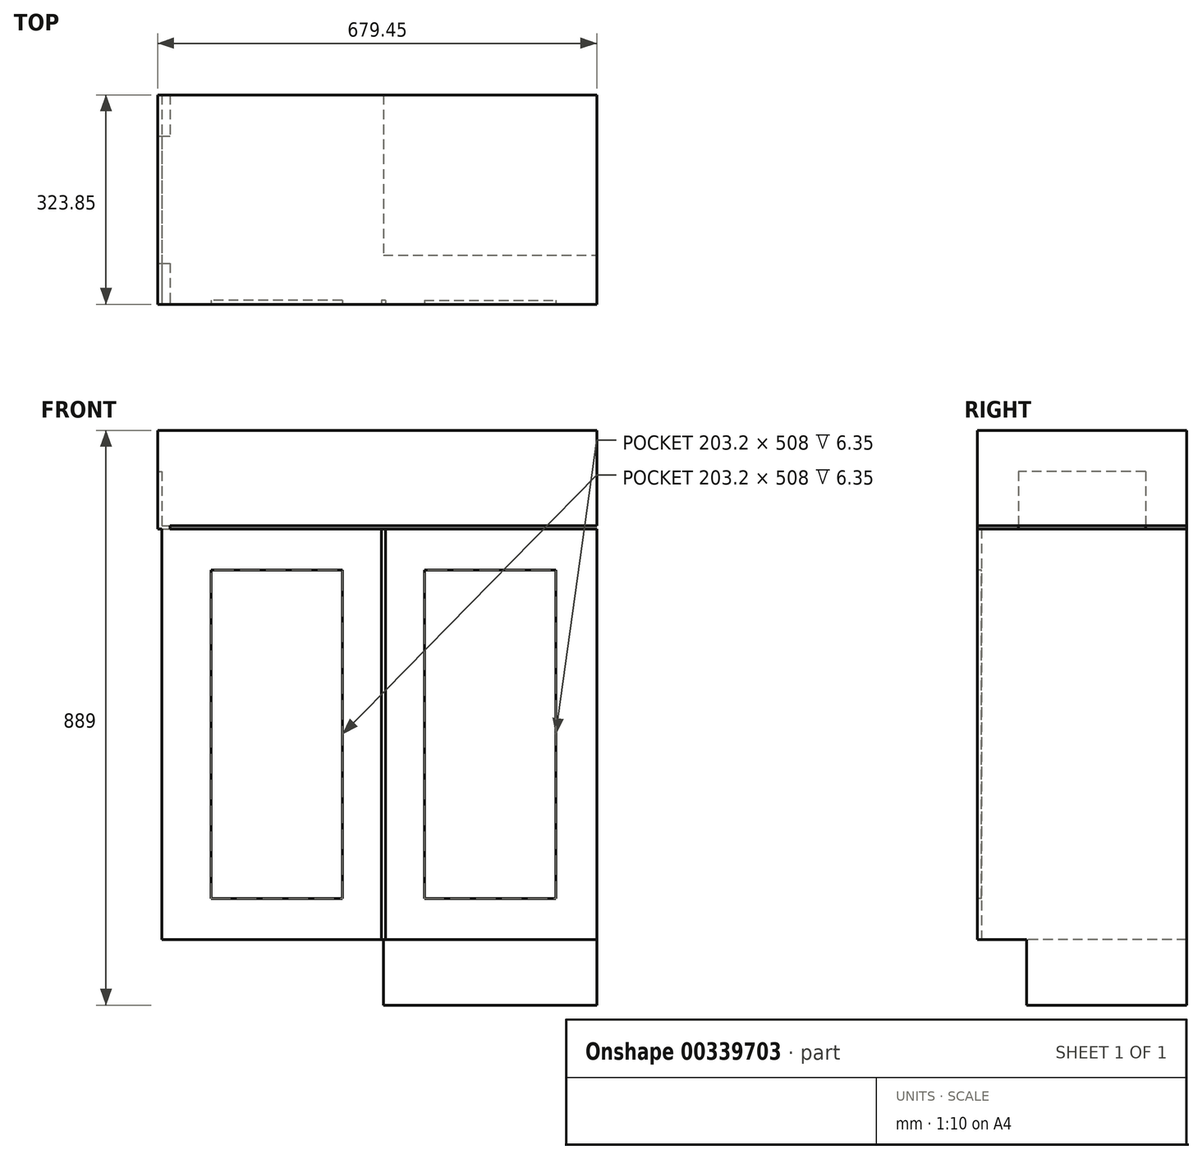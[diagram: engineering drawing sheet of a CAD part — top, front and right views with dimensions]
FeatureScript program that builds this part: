
annotation { "Feature Type Name" : "Feature", "Feature Type Description" : "" }
export const myFeature = defineFeature(function(context is Context, id is Id, definition is map)
    precondition{}
    {
        {
            var Q0;
            Q0=qCreatedBy(makeId("Front.planeOp"),FACE);
            var sketch = newSketch(context, id + "F0", { "sketchPlane" : qUnion([Q0])});
            skLineSegment(sketch, "E0.bottom", {"start": v(0, 0) * mm, "end": v(-330.2, 0) * mm});
            skLineSegment(sketch, "E0.top", {"start": v(0, 635) * mm, "end": v(-330.2, 635) * mm});
            skLineSegment(sketch, "E0.left", {"start": v(0, 0) * mm, "end": v(0, 635) * mm});
            skLineSegment(sketch, "E0.right", {"start": v(-330.2, 0) * mm, "end": v(-330.2, 635) * mm});
            skLineSegment(sketch, "E1.0", {"start": v(-63.5, 571.5) * mm, "end": v(-266.7, 571.5) * mm});
            skLineSegment(sketch, "E1.1", {"start": v(-63.5, 63.5) * mm, "end": v(-63.5, 571.5) * mm});
            skLineSegment(sketch, "E1.2", {"start": v(-63.5, 63.5) * mm, "end": v(-266.7, 63.5) * mm});
            skLineSegment(sketch, "E1.3", {"start": v(-266.7, 63.5) * mm, "end": v(-266.7, 571.5) * mm});
            skLineSegment(sketch, "E2.bottom", {"start": v(-330.2, 0) * mm, "end": v(0, 0) * mm});
            skLineSegment(sketch, "E2.top", {"start": v(-330.2, -101.6) * mm, "end": v(0, -101.6) * mm});
            skLineSegment(sketch, "E2.left", {"start": v(-330.2, 0) * mm, "end": v(-330.2, -101.6) * mm});
            skLineSegment(sketch, "E2.right", {"start": v(0, 0) * mm, "end": v(0, -101.6) * mm});
            skLineSegment(sketch, "E3.bottom", {"start": v(-330.2, 635) * mm, "end": v(0, 635) * mm});
            skLineSegment(sketch, "E3.top", {"start": v(-330.2, 787.4) * mm, "end": v(0, 787.4) * mm});
            skLineSegment(sketch, "E3.left", {"start": v(-330.2, 635) * mm, "end": v(-330.2, 787.4) * mm});
            skLineSegment(sketch, "E3.right", {"start": v(0, 635) * mm, "end": v(0, 787.4) * mm});
            skLineSegment(sketch, "E4.top", {"start": v(-330.2, 640.08) * mm, "end": v(0, 640.08) * mm});
            skLineSegment(sketch, "E4.left", {"start": v(-330.2, 635) * mm, "end": v(-330.2, 640.08) * mm});
            skLineSegment(sketch, "E4.right", {"start": v(0, 635) * mm, "end": v(0, 640.08) * mm});
            skLineSegment(sketch, "E5.MirrorCS", {"start": v(330.2, 635) * mm, "end": v(330.2, 640.08) * mm});
            skLineSegment(sketch, "E6.MirrorCS", {"start": v(0, 635) * mm, "end": v(330.2, 635) * mm});
            skLineSegment(sketch, "E7.MirrorCS", {"start": v(330.2, 635) * mm, "end": v(0, 635) * mm});
            skLineSegment(sketch, "E8.MirrorCS", {"start": v(0, 0) * mm, "end": v(330.2, 0) * mm});
            skLineSegment(sketch, "E9.MirrorCS", {"start": v(330.2, 0) * mm, "end": v(330.2, -101.6) * mm});
            skLineSegment(sketch, "E10.MirrorCS", {"start": v(330.2, -101.6) * mm, "end": v(0, -101.6) * mm});
            skLineSegment(sketch, "E11.MirrorCS", {"start": v(330.2, 0) * mm, "end": v(0, 0) * mm});
            skLineSegment(sketch, "E12.MirrorCS", {"start": v(266.7, 63.5) * mm, "end": v(266.7, 571.5) * mm});
            skLineSegment(sketch, "E13.MirrorCS", {"start": v(63.5, 63.5) * mm, "end": v(266.7, 63.5) * mm});
            skLineSegment(sketch, "E14.MirrorCS", {"start": v(63.5, 63.5) * mm, "end": v(63.5, 571.5) * mm});
            skLineSegment(sketch, "E15.MirrorCS", {"start": v(63.5, 571.5) * mm, "end": v(266.7, 571.5) * mm});
            skLineSegment(sketch, "E16.MirrorCS", {"start": v(330.2, 0) * mm, "end": v(330.2, 635) * mm});
            skLineSegment(sketch, "E17.MirrorCS", {"start": v(330.2, 635) * mm, "end": v(330.2, 787.4) * mm});
            skLineSegment(sketch, "E18.MirrorCS", {"start": v(330.2, 640.08) * mm, "end": v(0, 640.08) * mm});
            skLineSegment(sketch, "E19.MirrorCS", {"start": v(330.2, 787.4) * mm, "end": v(0, 787.4) * mm});
            skLineSegment(sketch, "E20", {"start": v(-3.18, 635) * mm, "end": v(-3.17, 0) * mm});
            skLineSegment(sketch, "E21", {"start": v(3.17, 635) * mm, "end": v(3.18, 0) * mm});
            skSolve(sketch);
        }
        {
            var Q0;
            Q0=makeQuery(id+"F0.imprint","IMPRINT",FACE,{"disambiguationData":[TD([[makeQuery(id+"F0.imprint","IMPRINT",EDGE,{"derivedFrom":sQuery(id+"F0.wireOp",EDGE,"E1.0")}),1.0]])]});
            var Q1;
            Q1=makeQuery(id+"F0.imprint","IMPRINT",FACE,{"disambiguationData":[TD([[makeQuery(id+"F0.imprint","IMPRINT",EDGE,{"derivedFrom":sQuery(id+"F0.wireOp",EDGE,"E2.bottom")}),-1.0]])]});
            var Q2;
            Q2=makeQuery(id+"F0.imprint","IMPRINT",FACE,{"disambiguationData":[TD([[makeQuery(id+"F0.imprint","IMPRINT",EDGE,{"derivedFrom":sQuery(id+"F0.wireOp",EDGE,"E0.left")}),1.0]])]});
            var Q3;
            {var subQ0=sQuery(id+"F0.wireOp",EDGE,"E3.top");Q3=makeQuery(id+"F0.imprint","IMPRINT",FACE,{"disambiguationData":[TD([[makeQuery(id+"F0.imprint","IMPRINT",EDGE,{"derivedFrom":subQ0}),-1.0]])]});}
            var Q4;
            {var subQ0=sQuery(id+"F0.wireOp",EDGE,"E3.bottom");Q4=makeQuery(id+"F0.imprint","IMPRINT",FACE,{"disambiguationData":[TD([[makeQuery(id+"F0.imprint","IMPRINT",EDGE,{"derivedFrom":subQ0}),1.0]])]});}
            var Q5;
            Q5=makeQuery(id+"F0.imprint","IMPRINT",FACE,{"disambiguationData":[TD([[makeQuery(id+"F0.imprint","IMPRINT",EDGE,{"derivedFrom":sQuery(id+"F0.wireOp",EDGE,"E12.MirrorCS")}),1.0]])]});
            var Q6;
            {var subQ2=sQuery(id+"F0.wireOp",EDGE,"E18.MirrorCS");Q6=makeQuery(id+"F0.imprint","IMPRINT",FACE,{"disambiguationData":[TD([[makeQuery(id+"F0.imprint","IMPRINT",EDGE,{"derivedFrom":subQ2}),-1.0]])]});}
            var Q7;
            Q7=makeQuery(id+"F0.imprint","IMPRINT",FACE,{"disambiguationData":[TD([[makeQuery(id+"F0.imprint","IMPRINT",EDGE,{"derivedFrom":sQuery(id+"F0.wireOp",EDGE,"E2.right")}),1.0]])]});
            var Q8;
            Q8=makeQuery(id+"F0.imprint","IMPRINT",FACE,{"disambiguationData":[TD([[makeQuery(id+"F0.imprint","IMPRINT",EDGE,{"derivedFrom":sQuery(id+"F0.wireOp",EDGE,"E0.left")}),-1.0]])]});
            var Q9;
            {var subQ0=sQuery(id+"F0.wireOp",EDGE,"E7.MirrorCS");Q9=makeQuery(id+"F0.imprint","IMPRINT",FACE,{"disambiguationData":[TD([[makeQuery(id+"F0.imprint","IMPRINT",EDGE,{"derivedFrom":subQ0}),-1.0]])]});}
            var Q10;
            {var subQ0=sQuery(id+"F0.wireOp",EDGE,"E0.right");Q10=makeQuery(id+"F0.imprint","IMPRINT",FACE,{"disambiguationData":[TD([[makeQuery(id+"F0.imprint","IMPRINT",EDGE,{"derivedFrom":subQ0}),-1.0]])]});}
            var Q11;
            Q11=makeQuery(id+"F0.imprint","IMPRINT",FACE,{"disambiguationData":[TD([[makeQuery(id+"F0.imprint","IMPRINT",EDGE,{"derivedFrom":sQuery(id+"F0.wireOp",EDGE,"E12.MirrorCS")}),-1.0]])]});
            extrude(context, id + "F1", {"entities" : qUnion([Q0, Q1, Q2, Q3, Q4, Q5, Q6, Q7, Q8, Q9, Q10, Q11]), "oppositeDirection" : true, "depth" : 323.85 * mm, "offsetDistance" : 25.4 * mm});
        }
        {
            var Q0;
            Q0=makeQuery(id+"F0.imprint","IMPRINT",FACE,{"disambiguationData":[TD([[makeQuery(id+"F0.imprint","IMPRINT",EDGE,{"derivedFrom":sQuery(id+"F0.wireOp",EDGE,"E1.0")}),1.0]])]});
            var Q1;
            Q1=makeQuery(id+"F0.imprint","IMPRINT",FACE,{"disambiguationData":[TD([[makeQuery(id+"F0.imprint","IMPRINT",EDGE,{"derivedFrom":sQuery(id+"F0.wireOp",EDGE,"E3.bottom")}),1.0]])]});
            var Q2;
            Q2=makeQuery(id+"F0.imprint","IMPRINT",FACE,{"disambiguationData":[TD([[makeQuery(id+"F0.imprint","IMPRINT",EDGE,{"derivedFrom":sQuery(id+"F0.wireOp",EDGE,"E12.MirrorCS")}),1.0]])]});
            var Q3;
            {var subQ0=sQuery(id+"F0.wireOp",EDGE,"E7.MirrorCS");Q3=makeQuery(id+"F0.imprint","IMPRINT",FACE,{"disambiguationData":[TD([[makeQuery(id+"F0.imprint","IMPRINT",EDGE,{"derivedFrom":subQ0}),-1.0]])]});}
            var Q4;
            {var subQ0=sQuery(id+"F0.wireOp",EDGE,"E0.left");Q4=makeQuery(id+"F0.imprint","IMPRINT",FACE,{"disambiguationData":[TD([[makeQuery(id+"F0.imprint","IMPRINT",EDGE,{"derivedFrom":subQ0}),1.0]])]});}
            var Q5;
            {var subQ0=sQuery(id+"F0.wireOp",EDGE,"E0.left");Q5=makeQuery(id+"F0.imprint","IMPRINT",FACE,{"disambiguationData":[TD([[makeQuery(id+"F0.imprint","IMPRINT",EDGE,{"derivedFrom":subQ0}),-1.0]])]});}
            extrude(context, id + "F2", {"entities" : qUnion([Q0, Q1, Q2, Q3, Q4, Q5]), "operationType" : NewBodyOperationType.REMOVE, "oppositeDirection" : true, "depth" : 6.35 * mm});
        }
        {
            var Q0;
            Q0=makeQuery(id+"F0.imprint","IMPRINT",FACE,{"disambiguationData":[TD([[makeQuery(id+"F0.imprint","IMPRINT",EDGE,{"derivedFrom":sQuery(id+"F0.wireOp",EDGE,"E2.bottom")}),-1.0]])]});
            var Q1;
            Q1=makeQuery(id+"F0.imprint","IMPRINT",FACE,{"disambiguationData":[TD([[makeQuery(id+"F0.imprint","IMPRINT",EDGE,{"derivedFrom":sQuery(id+"F0.wireOp",EDGE,"E2.right")}),1.0]])]});
            extrude(context, id + "F3", {"entities" : qUnion([Q0, Q1]), "operationType" : NewBodyOperationType.REMOVE, "oppositeDirection" : true, "depth" : 76.2 * mm});
        }
        {
            var Q0;
            Q0=makeQuery(id+"F1.opExtrude","SWEPT_FACE",FACE,{"disambiguationData":[OSD([sQuery(id+"F0.wireOp",EDGE,"E0.right"),sQuery(id+"F0.wireOp",EDGE,"E2.left"),sQuery(id+"F0.wireOp",EDGE,"E3.left"),sQuery(id+"F0.wireOp",EDGE,"E4.left")])]});
            var sketch = newSketch(context, id + "F4", { "sketchPlane" : qUnion([Q0])});
            skLineSegment(sketch, "E22.bottom", {"start": v(-323.85, 787.4) * mm, "end": v(0, 787.4) * mm});
            skLineSegment(sketch, "E22.top", {"start": v(-323.85, 0) * mm, "end": v(0, 0) * mm});
            skLineSegment(sketch, "E22.left", {"start": v(-323.85, 787.4) * mm, "end": v(-323.85, 0) * mm});
            skLineSegment(sketch, "E22.right", {"start": v(0, 787.4) * mm, "end": v(0, 0) * mm});
            skLineSegment(sketch, "E23.0", {"start": v(-260.35, 723.9) * mm, "end": v(-63.5, 723.9) * mm});
            skLineSegment(sketch, "E23.1", {"start": v(-260.35, 723.9) * mm, "end": v(-260.35, 63.5) * mm});
            skLineSegment(sketch, "E23.2", {"start": v(-260.35, 63.5) * mm, "end": v(-63.5, 63.5) * mm});
            skLineSegment(sketch, "E23.3", {"start": v(-63.5, 723.9) * mm, "end": v(-63.5, 63.5) * mm});
            skSolve(sketch);
        }
        {
            var Q0;
            Q0=makeQuery(id+"F4.imprint","IMPRINT",FACE,{"disambiguationData":[TD([[makeQuery(id+"F4.imprint","IMPRINT",EDGE,{"derivedFrom":sQuery(id+"F4.wireOp",EDGE,"E22.bottom")}),-1.0]])]});
            extrude(context, id + "F5", {"entities" : qUnion([Q0]), "operationType" : NewBodyOperationType.ADD, "depth" : 19.05 * mm, "offsetDistance" : 25.4 * mm});
        }
        {
            var Q0;
            Q0=makeQuery(id+"F5.boolean.opBoolean","SPLIT",FACE,{"disambiguationData":[TD([makeQuery(id+"F5.opExtrude","SWEPT_FACE",FACE,{"disambiguationData":[OSD([sQuery(id+"F4.wireOp",EDGE,"E23.0")])]})])],"derivedFrom":makeQuery(id+"F1.opExtrude","SWEPT_FACE",FACE,{"disambiguationData":[OSD([sQuery(id+"F0.wireOp",EDGE,"E0.right"),sQuery(id+"F0.wireOp",EDGE,"E2.left"),sQuery(id+"F0.wireOp",EDGE,"E3.left"),sQuery(id+"F0.wireOp",EDGE,"E4.left")])]})});
            extrude(context, id + "F6", {"entities" : qUnion([Q0]), "operationType" : NewBodyOperationType.ADD, "depth" : 12.7 * mm, "offsetDistance" : 25.4 * mm});
        }
    });
